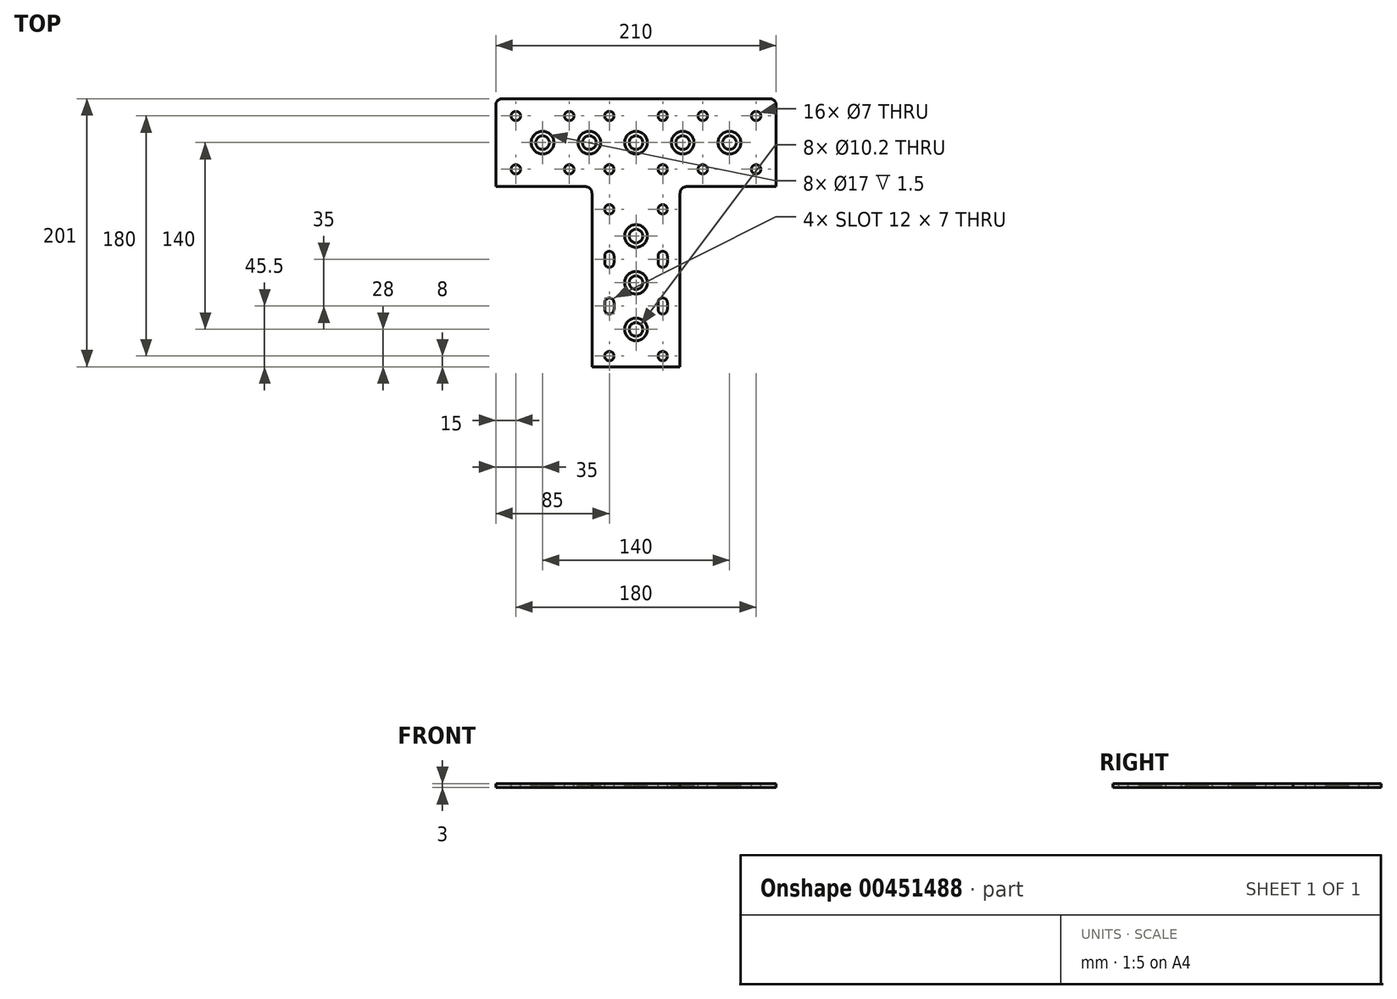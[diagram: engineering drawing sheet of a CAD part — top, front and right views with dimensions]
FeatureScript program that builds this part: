
annotation { "Feature Type Name" : "Feature", "Feature Type Description" : "" }
export const myFeature = defineFeature(function(context is Context, id is Id, definition is map)
    precondition{}
    {
        {
            var Q0;
            Q0=qCreatedBy(makeId("Top.planeOp"),FACE);
            var sketch = newSketch(context, id + "F0", { "sketchPlane" : qUnion([Q0])});
            skLineSegment(sketch, "E0.bottom", {"start": v(105, -100.5) * mm, "end": v(-105, -100.5) * mm});
            skLineSegment(sketch, "E0.top", {"start": v(105, 100.5) * mm, "end": v(-105, 100.5) * mm});
            skLineSegment(sketch, "E0.left", {"start": v(105, -100.5) * mm, "end": v(105, 100.5) * mm});
            skLineSegment(sketch, "E0.right", {"start": v(-105, -100.5) * mm, "end": v(-105, 100.5) * mm});
            skPoint(sketch, "E0.middle", {"position": v(0, 0) * mm});
            skSolve(sketch);
        }
        {
            var Q0;
            Q0=qSketchRegion(id+"F0",true);
            extrude(context, id + "F1", {"entities" : qUnion([Q0]), "oppositeDirection" : true, "depth" : 3 * mm});
        }
        {
            var Q0;
            Q0=makeQuery(id+"F1.opExtrude","CAP_FACE",FACE,{"disambiguationData":[OSD([sQuery(id+"F0.wireOp",EDGE,"E0.bottom"),sQuery(id+"F0.wireOp",EDGE,"E0.top"),sQuery(id+"F0.wireOp",EDGE,"E0.left"),sQuery(id+"F0.wireOp",EDGE,"E0.right")])],"isStart":true});
            var sketch = newSketch(context, id + "F2", { "sketchPlane" : qUnion([Q0])});
            skLineSegment(sketch, "E1.bottom", {"start": v(105, -100.5) * mm, "end": v(33, -100.5) * mm});
            skLineSegment(sketch, "E1.top", {"start": v(105, 34.5) * mm, "end": v(33, 34.5) * mm});
            skLineSegment(sketch, "E1.left", {"start": v(105, -100.5) * mm, "end": v(105, 34.5) * mm});
            skLineSegment(sketch, "E1.right", {"start": v(33, -100.5) * mm, "end": v(33, 34.5) * mm});
            skLineSegment(sketch, "E2.MirrorCS", {"start": v(-33, -100.5) * mm, "end": v(-33, 34.5) * mm});
            skLineSegment(sketch, "E3.MirrorCS", {"start": v(-105, 34.5) * mm, "end": v(-33, 34.5) * mm});
            skLineSegment(sketch, "E4.MirrorCS", {"start": v(-105, -100.5) * mm, "end": v(-105, 34.5) * mm});
            skLineSegment(sketch, "E5.MirrorCS", {"start": v(-105, -100.5) * mm, "end": v(-33, -100.5) * mm});
            skSolve(sketch);
        }
        {
            var Q0;
            Q0=qSketchRegion(id+"F2",true);
            extrude(context, id + "F3", {"entities" : qUnion([Q0]), "operationType" : NewBodyOperationType.REMOVE, "endBound" : BoundingType.THROUGH_ALL, "oppositeDirection" : true, "depth" : 25 * mm});
        }
        {
            var Q0;
            Q0=makeQuery(id+"F3.boolean.opBoolean","COPY",EDGE,{"derivedFrom":makeQuery(id+"F3.opExtrude","SWEPT_EDGE",EDGE,{"disambiguationData":[OSD([sQuery(id+"F0.wireOp",EDGE,"E0.bottom"),sQuery(id+"F2.wireOp",EDGE,"E1.bottom"),sQuery(id+"F2.wireOp",EDGE,"E1.right")])]})});
            var Q1;
            Q1=makeQuery(id+"F3.boolean.opBoolean","COPY",EDGE,{"derivedFrom":makeQuery(id+"F3.opExtrude","SWEPT_EDGE",EDGE,{"disambiguationData":[OSD([sQuery(id+"F2.wireOp",EDGE,"E1.top"),sQuery(id+"F2.wireOp",EDGE,"E1.right")])]})});
            var Q2;
            Q2=makeQuery(id+"F3.boolean.opBoolean","COPY",EDGE,{"derivedFrom":makeQuery(id+"F3.opExtrude","SWEPT_EDGE",EDGE,{"disambiguationData":[OSD([sQuery(id+"F0.wireOp",EDGE,"E0.left"),sQuery(id+"F2.wireOp",EDGE,"E1.top"),sQuery(id+"F2.wireOp",EDGE,"E1.left")])]})});
            var Q3;
            Q3=makeQuery(id+"F1.opExtrude","SWEPT_EDGE",EDGE,{"disambiguationData":[OSD([sQuery(id+"F0.wireOp",EDGE,"E0.top"),sQuery(id+"F0.wireOp",EDGE,"E0.left")])]});
            var Q4;
            Q4=makeQuery(id+"F3.boolean.opBoolean","COPY",EDGE,{"derivedFrom":makeQuery(id+"F3.opExtrude","SWEPT_EDGE",EDGE,{"disambiguationData":[OSD([sQuery(id+"F0.wireOp",EDGE,"E0.bottom"),sQuery(id+"F2.wireOp",EDGE,"E2.MirrorCS"),sQuery(id+"F2.wireOp",EDGE,"E5.MirrorCS")])]})});
            var Q5;
            Q5=makeQuery(id+"F3.boolean.opBoolean","COPY",EDGE,{"derivedFrom":makeQuery(id+"F3.opExtrude","SWEPT_EDGE",EDGE,{"disambiguationData":[OSD([sQuery(id+"F2.wireOp",EDGE,"E2.MirrorCS"),sQuery(id+"F2.wireOp",EDGE,"E3.MirrorCS")])]})});
            var Q6;
            Q6=makeQuery(id+"F3.boolean.opBoolean","COPY",EDGE,{"derivedFrom":makeQuery(id+"F3.opExtrude","SWEPT_EDGE",EDGE,{"disambiguationData":[OSD([sQuery(id+"F0.wireOp",EDGE,"E0.right"),sQuery(id+"F2.wireOp",EDGE,"E3.MirrorCS"),sQuery(id+"F2.wireOp",EDGE,"E4.MirrorCS")])]})});
            var Q7;
            Q7=makeQuery(id+"F1.opExtrude","SWEPT_EDGE",EDGE,{"disambiguationData":[OSD([sQuery(id+"F0.wireOp",EDGE,"E0.top"),sQuery(id+"F0.wireOp",EDGE,"E0.right")])]});
            fillet(context, id + "F4", {"entities" : qUnion([Q0, Q1, Q2, Q3, Q4, Q5, Q6, Q7]), "radius" : 5 * mm, "tangentPropagation" : true, "allowEdgeOverflow" : false});
        }
        {
            var Q0;
            Q0=makeQuery(id+"F1.opExtrude","CAP_FACE",FACE,{"disambiguationData":[OSD([sQuery(id+"F0.wireOp",EDGE,"E0.bottom"),sQuery(id+"F0.wireOp",EDGE,"E0.top"),sQuery(id+"F0.wireOp",EDGE,"E0.left"),sQuery(id+"F0.wireOp",EDGE,"E0.right")])],"isStart":true});
            var sketch = newSketch(context, id + "F5", { "sketchPlane" : qUnion([Q0])});
            skCircle(sketch, "E6", {"center": v(-90, 87.5) * mm, "radius": 3.5 * mm});
            skCircle(sketch, "E7", {"center": v(-90, 47.5) * mm, "radius": 3.5 * mm});
            skCircle(sketch, "E8", {"center": v(-50, 87.5) * mm, "radius": 3.5 * mm});
            skCircle(sketch, "E9", {"center": v(-50, 47.5) * mm, "radius": 3.5 * mm});
            skCircle(sketch, "E10", {"center": v(-70, 67.5) * mm, "radius": 5.1 * mm});
            skCircle(sketch, "E11", {"center": v(-20, 87.5) * mm, "radius": 3.5 * mm});
            skCircle(sketch, "E12", {"center": v(20, 87.5) * mm, "radius": 3.5 * mm});
            skCircle(sketch, "E13", {"center": v(50, 87.5) * mm, "radius": 3.5 * mm});
            skCircle(sketch, "E14", {"center": v(90, 87.5) * mm, "radius": 3.5 * mm});
            skCircle(sketch, "E15", {"center": v(-20, 47.5) * mm, "radius": 3.5 * mm});
            skCircle(sketch, "E16", {"center": v(20, 47.5) * mm, "radius": 3.5 * mm});
            skCircle(sketch, "E17", {"center": v(50, 47.5) * mm, "radius": 3.5 * mm});
            skCircle(sketch, "E18", {"center": v(90, 47.5) * mm, "radius": 3.5 * mm});
            skCircle(sketch, "E19.1.0.0", {"center": v(-35, 67.5) * mm, "radius": 5.1 * mm});
            skCircle(sketch, "E19.2.0.0", {"center": v(0, 67.5) * mm, "radius": 5.1 * mm});
            skCircle(sketch, "E19.3.0.0", {"center": v(35, 67.5) * mm, "radius": 5.1 * mm});
            skCircle(sketch, "E19.4.0.0", {"center": v(70, 67.5) * mm, "radius": 5.1 * mm});
            skLineSegment(sketch, "E19.direction1", {"start": v(-70, 67.5) * mm, "end": v(-35, 67.5) * mm, "construction": true});
            skCircle(sketch, "E20", {"center": v(-20, 17.5) * mm, "radius": 3.5 * mm});
            skCircle(sketch, "E21", {"center": v(-20, -92.5) * mm, "radius": 3.5 * mm});
            skLineSegment(sketch, "E22", {"start": v(-20, -17.5) * mm, "end": v(-20, -22.5) * mm, "construction": true});
            skLineSegment(sketch, "E23", {"start": v(-20, -52.5) * mm, "end": v(-20, -57.5) * mm, "construction": true});
            skArc(sketch, "E24.0.startCap", {"start": v(-23.5, -17.5) * mm, "mid": v(-20, -14) * mm, "end": v(-16.5, -17.5) * mm});
            skArc(sketch, "E24.0.endCap", {"start": v(-16.5, -22.5) * mm, "mid": v(-20, -26) * mm, "end": v(-23.5, -22.5) * mm});
            skLineSegment(sketch, "E24.0.left", {"start": v(-16.5, -17.5) * mm, "end": v(-16.5, -22.5) * mm});
            skLineSegment(sketch, "E24.0.right", {"start": v(-23.5, -17.5) * mm, "end": v(-23.5, -22.5) * mm});
            skArc(sketch, "E24.1.startCap", {"start": v(-23.5, -52.5) * mm, "mid": v(-20, -49) * mm, "end": v(-16.5, -52.5) * mm});
            skArc(sketch, "E24.1.endCap", {"start": v(-16.5, -57.5) * mm, "mid": v(-20, -61) * mm, "end": v(-23.5, -57.5) * mm});
            skLineSegment(sketch, "E24.1.left", {"start": v(-16.5, -52.5) * mm, "end": v(-16.5, -57.5) * mm});
            skLineSegment(sketch, "E24.1.right", {"start": v(-23.5, -52.5) * mm, "end": v(-23.5, -57.5) * mm});
            skCircle(sketch, "E25.MirrorC", {"center": v(20, -92.5) * mm, "radius": 3.5 * mm});
            skArc(sketch, "E26.MirrorCS", {"start": v(16.5, -57.5) * mm, "mid": v(20, -61) * mm, "end": v(23.5, -57.5) * mm});
            skArc(sketch, "E27.MirrorCS", {"start": v(23.5, -52.5) * mm, "mid": v(20, -49) * mm, "end": v(16.5, -52.5) * mm});
            skLineSegment(sketch, "E28.MirrorCS", {"start": v(23.5, -52.5) * mm, "end": v(23.5, -57.5) * mm});
            skLineSegment(sketch, "E29.MirrorCS", {"start": v(16.5, -52.5) * mm, "end": v(16.5, -57.5) * mm});
            skArc(sketch, "E30.MirrorCS", {"start": v(23.5, -17.5) * mm, "mid": v(20, -14) * mm, "end": v(16.5, -17.5) * mm});
            skLineSegment(sketch, "E31.MirrorCS", {"start": v(16.5, -17.5) * mm, "end": v(16.5, -22.5) * mm});
            skArc(sketch, "E32.MirrorCS", {"start": v(16.5, -22.5) * mm, "mid": v(20, -26) * mm, "end": v(23.5, -22.5) * mm});
            skLineSegment(sketch, "E33.MirrorCS", {"start": v(23.5, -17.5) * mm, "end": v(23.5, -22.5) * mm});
            skCircle(sketch, "E34.MirrorC", {"center": v(20, 17.5) * mm, "radius": 3.5 * mm});
            skCircle(sketch, "E35", {"center": v(0, -2.5) * mm, "radius": 5.1 * mm});
            skCircle(sketch, "E36", {"center": v(0, -37.5) * mm, "radius": 5.1 * mm});
            skCircle(sketch, "E37", {"center": v(0, -72.5) * mm, "radius": 5.1 * mm});
            skSolve(sketch);
        }
        {
            var Q0;
            Q0=qSketchRegion(id+"F5",true);
            extrude(context, id + "F6", {"entities" : qUnion([Q0]), "operationType" : NewBodyOperationType.REMOVE, "endBound" : BoundingType.THROUGH_ALL, "oppositeDirection" : true, "depth" : 25 * mm});
        }
        {
            var Q0;
            Q0=makeQuery(id+"F1.opExtrude","CAP_FACE",FACE,{"disambiguationData":[OSD([sQuery(id+"F0.wireOp",EDGE,"E0.bottom"),sQuery(id+"F0.wireOp",EDGE,"E0.top"),sQuery(id+"F0.wireOp",EDGE,"E0.left"),sQuery(id+"F0.wireOp",EDGE,"E0.right")])],"isStart":true});
            var sketch = newSketch(context, id + "F7", { "sketchPlane" : qUnion([Q0])});
            skCircle(sketch, "E38", {"center": v(-70, 67.5) * mm, "radius": 8.5 * mm});
            skCircle(sketch, "E39.1.0.0", {"center": v(-35, 67.5) * mm, "radius": 8.5 * mm});
            skCircle(sketch, "E39.2.0.0", {"center": v(0, 67.5) * mm, "radius": 8.5 * mm});
            skCircle(sketch, "E39.3.0.0", {"center": v(35, 67.5) * mm, "radius": 8.5 * mm});
            skCircle(sketch, "E39.4.0.0", {"center": v(70, 67.5) * mm, "radius": 8.5 * mm});
            skLineSegment(sketch, "E39.direction1", {"start": v(-70, 67.5) * mm, "end": v(-35, 67.5) * mm, "construction": true});
            skCircle(sketch, "E40", {"center": v(0, -72.5) * mm, "radius": 8.5 * mm});
            skCircle(sketch, "E41.0.1.0", {"center": v(0, -37.5) * mm, "radius": 8.5 * mm});
            skCircle(sketch, "E41.0.2.0", {"center": v(0, -2.5) * mm, "radius": 8.5 * mm});
            skLineSegment(sketch, "E41.direction1", {"start": v(0, -72.5) * mm, "end": v(25, -72.5) * mm, "construction": true});
            skLineSegment(sketch, "E41.direction2", {"start": v(0, -72.5) * mm, "end": v(0, -37.5) * mm, "construction": true});
            skSolve(sketch);
        }
        {
            var Q0;
            Q0=qSketchRegion(id+"F7",true);
            extrude(context, id + "F8", {"entities" : qUnion([Q0]), "operationType" : NewBodyOperationType.REMOVE, "oppositeDirection" : true, "depth" : 1.5 * mm});
        }
    });
